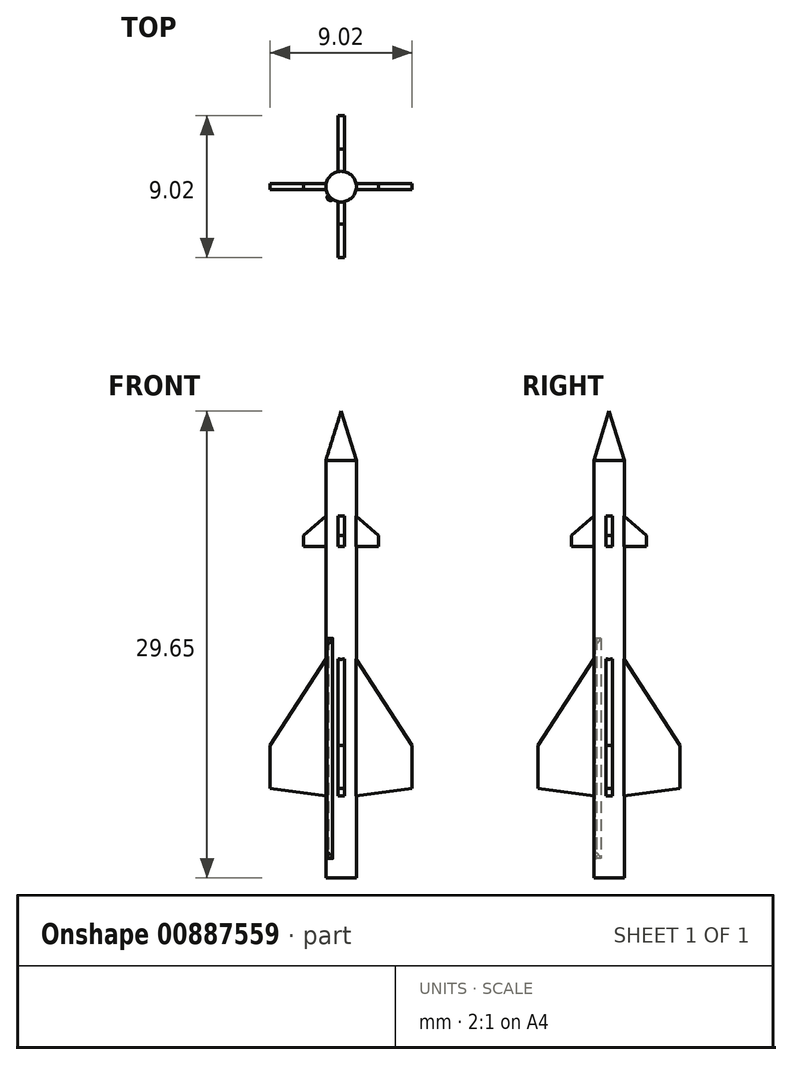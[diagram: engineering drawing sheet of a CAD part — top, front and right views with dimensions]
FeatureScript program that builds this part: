
annotation { "Feature Type Name" : "Feature", "Feature Type Description" : "" }
export const myFeature = defineFeature(function(context is Context, id is Id, definition is map)
    precondition{}
    {
        {
            var Q0;
            Q0=qCreatedBy(makeId("Front.planeOp"),FACE);
            var sketch = newSketch(context, id + "F0", { "sketchPlane" : qUnion([Q0])});
            skLineSegment(sketch, "E0", {"start": v(0, 0) * mm, "end": v(0, 29.65) * mm});
            skLineSegment(sketch, "E1", {"start": v(0.97, 26.53) * mm, "end": v(0.97, 0) * mm});
            skLineSegment(sketch, "E2", {"start": v(0.97, 0) * mm, "end": v(0, 0) * mm});
            skLineSegment(sketch, "E3", {"start": v(0, 29.65) * mm, "end": v(0.97, 26.53) * mm});
            skSolve(sketch);
        }
        {
            var Q0;
            Q0=makeQuery(id+"F0.imprint","IMPRINT",FACE,{"disambiguationData":[TD([[makeQuery(id+"F0.imprint","IMPRINT",EDGE,{"derivedFrom":sQuery(id+"F0.wireOp",EDGE,"E0")}),-1.0]])]});
            var Q1;
            Q1=sQuery(id+"F0.wireOp",EDGE,"E0");
            revolve(context, id + "F1", {"surfaceOperationType" : NewSurfaceOperationType.NEW, "entities" : qUnion([Q0]), "axis" : qUnion([Q1]), "revolveType" : RevolveType.FULL});
        }
        {
            var Q0;
            Q0=qCreatedBy(makeId("Front.planeOp"),FACE);
            var sketch = newSketch(context, id + "F2", { "sketchPlane" : qUnion([Q0])});
            skLineSegment(sketch, "E4.0", {"start": v(0.97, 26.53) * mm, "end": v(-0.97, 26.53) * mm, "construction": true});
            skLineSegment(sketch, "E5", {"start": v(0, 5.07) * mm, "end": v(4.51, 5.7) * mm});
            skLineSegment(sketch, "E6", {"start": v(4.51, 5.7) * mm, "end": v(4.51, 8.4) * mm});
            skLineSegment(sketch, "E7", {"start": v(4.51, 8.4) * mm, "end": v(0.97, 13.89) * mm});
            skLineSegment(sketch, "E8", {"start": v(0.4, 14.78) * mm, "end": v(0.4, 21.04) * mm});
            skLineSegment(sketch, "E9", {"start": v(0.4, 21.04) * mm, "end": v(2.38, 21.04) * mm});
            skLineSegment(sketch, "E10", {"start": v(2.38, 21.04) * mm, "end": v(2.38, 21.74) * mm});
            skLineSegment(sketch, "E11", {"start": v(2.37, 21.74) * mm, "end": v(0, 23.85) * mm});
            skLineSegment(sketch, "E12", {"start": v(0, 23.85) * mm, "end": v(0, 5.07) * mm});
            skLineSegment(sketch, "E13", {"start": v(0.97, 26.53) * mm, "end": v(0.97, 0) * mm, "construction": true});
            skPoint(sketch, "E14", {"position": v(0.97, 5.2) * mm});
            skPoint(sketch, "E15", {"position": v(0.97, 22.99) * mm});
            skLineSegment(sketch, "E16", {"start": v(0.97, 13.89) * mm, "end": v(0.4, 14.78) * mm});
            skSolve(sketch);
        }
        {
            var Q0;
            Q0=qSketchRegion(id+"F2",true);
            extrude(context, id + "F3", {"entities" : qUnion([Q0]), "operationType" : NewBodyOperationType.ADD, "oppositeDirection" : true, "depth" : .4 * mm, "offsetDistance" : 25 * mm, "symmetric" : true});
        }
        {
            var Q0;
            Q0=makeQuery(id+"F1.opRevolve","SWEPT_BODY",BODY,{"disambiguationData":[OSD([sQuery(id+"F0.wireOp",EDGE,"E0"),sQuery(id+"F0.wireOp",EDGE,"E1"),sQuery(id+"F0.wireOp",EDGE,"E2"),sQuery(id+"F0.wireOp",EDGE,"h1jDSi8t-veb7-85qg-XgDk-6E8DmZjBuz4r")])]});
            var Q1;
            Q1=makeQuery(id+"F1.opRevolve","SWEPT_FACE",FACE,{"disambiguationData":[OSD([sQuery(id+"F0.wireOp",EDGE,"E1")])]});
            circularPattern(context, id + "F4", {"operationType" : NewBodyOperationType.ADD, "entities" : qUnion([Q0]), "axis" : qUnion([Q1]), "angle" : 360 * degree, "instanceCount" : 4, "equalSpace" : true, "computeTransformsWithoutBuiltin" : true});
        }
        {
            var Q0;
            Q0=qCreatedBy(makeId("Top.planeOp"),FACE);
            cPlane(context, id + "F5", {"entities" : qUnion([Q0]), "cplaneType" : CPlaneType.OFFSET, "offset" : (240 / 144) * mm, "width" : 150 * mm, "height" : 150 * mm});
        }
        {
            var Q0;
            Q0=qCreatedBy(id+"F5.planeOp",FACE);
            var sketch = newSketch(context, id + "F6", { "sketchPlane" : qUnion([Q0])});
            skLineSegment(sketch, "E17", {"start": v(-0.83, -0.55) * mm, "end": v(-0.63, -0.35) * mm});
            skLineSegment(sketch, "E18", {"start": v(-0.63, -0.35) * mm, "end": v(-0.35, -0.63) * mm});
            skLineSegment(sketch, "E19", {"start": v(-0.35, -0.63) * mm, "end": v(-0.55, -0.83) * mm});
            skArc(sketch, "E20", {"start": v(-0.83, -0.55) * mm, "mid": v(-0.83, -0.83) * mm, "end": v(-0.55, -0.83) * mm});
            skLineSegment(sketch, "E21", {"start": v(-0.5, -0.5) * mm, "end": v(0, 0) * mm, "construction": true});
            skLineSegment(sketch, "E22", {"start": v(0, 0) * mm, "end": v(-0.48, 0) * mm, "construction": true});
            skSolve(sketch);
        }
        {
            var Q0;
            Q0=makeQuery(id+"F6.imprint","IMPRINT",FACE,{"disambiguationData":[TD([[makeQuery(id+"F6.imprint","IMPRINT",EDGE,{"derivedFrom":sQuery(id+"F6.wireOp",EDGE,"E17")}),-1.0]])]});
            extrude(context, id + "F7", {"entities" : qUnion([Q0]), "operationType" : NewBodyOperationType.ADD, "depth" : (1890 / 144) * mm, "offsetDistance" : 25 * mm});
        }
        {
            var Q0;
            Q0=makeQuery(id+"F7.boolean.opBoolean","INTERSECT",EDGE,{"derivedFrom":[makeQuery(id+"F1.opRevolve","SWEPT_FACE",FACE,{"disambiguationData":[OSD([sQuery(id+"F0.wireOp",EDGE,"E1")])]}),makeQuery(id+"F7.opExtrude","CAP_FACE",FACE,{"disambiguationData":[OSD([sQuery(id+"F6.wireOp",EDGE,"E17"),sQuery(id+"F6.wireOp",EDGE,"E18"),sQuery(id+"F6.wireOp",EDGE,"E19"),sQuery(id+"F6.wireOp",EDGE,"E20")])],"isStart":false})]});
            var Q1;
            Q1=makeQuery(id+"F7.boolean.opBoolean","INTERSECT",EDGE,{"derivedFrom":[makeQuery(id+"F1.opRevolve","SWEPT_FACE",FACE,{"disambiguationData":[OSD([sQuery(id+"F0.wireOp",EDGE,"E1")])]}),makeQuery(id+"F7.opExtrude","CAP_FACE",FACE,{"disambiguationData":[OSD([sQuery(id+"F6.wireOp",EDGE,"E17"),sQuery(id+"F6.wireOp",EDGE,"E18"),sQuery(id+"F6.wireOp",EDGE,"E19"),sQuery(id+"F6.wireOp",EDGE,"E20")])],"isStart":true})]});
            chamfer(context, id + "F8", {"entities" : qUnion([Q0, Q1]), "chamferType" : ChamferType.OFFSET_ANGLE, "width" : .25 * mm, "oppositeDirection" : true, "angle" : 60 * degree, "tangentPropagation" : true});
        }
    });
